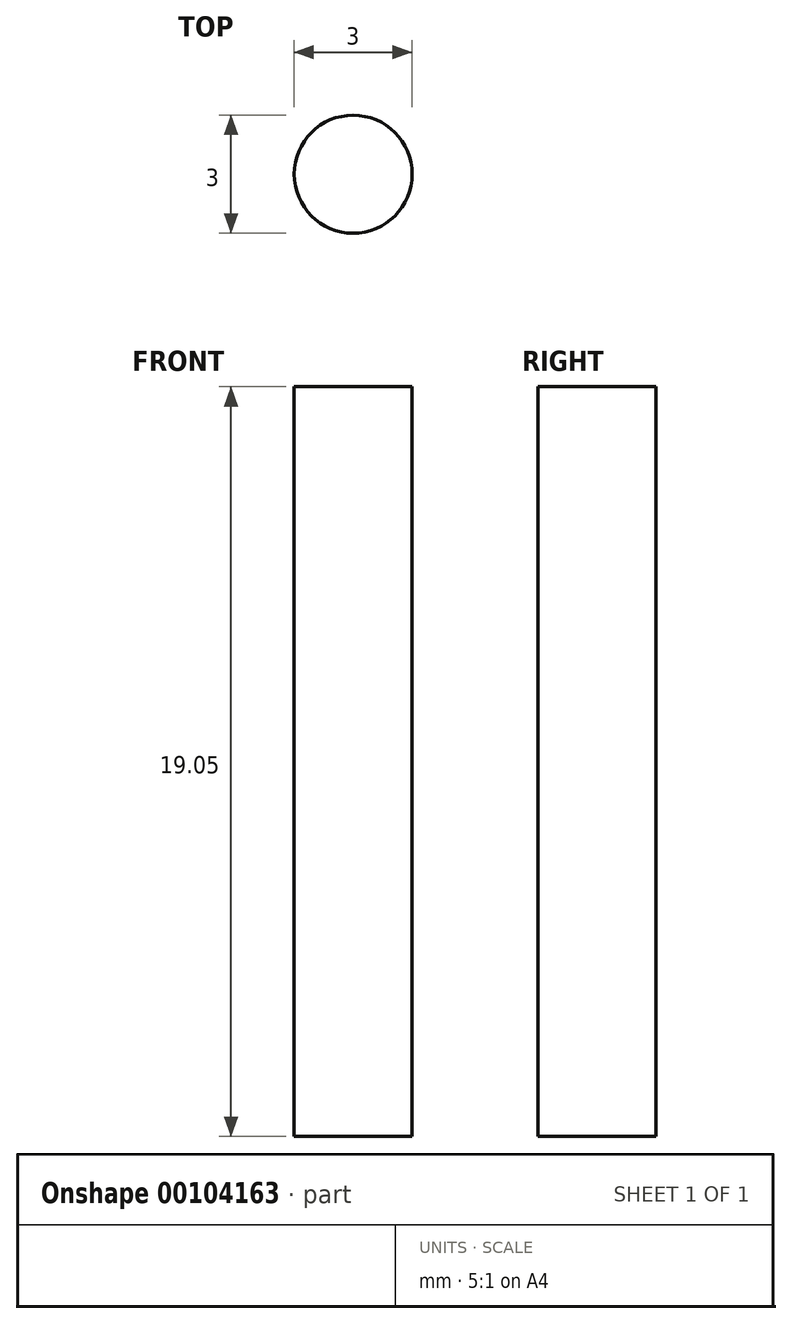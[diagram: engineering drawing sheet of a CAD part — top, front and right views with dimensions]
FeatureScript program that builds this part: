
annotation { "Feature Type Name" : "Feature", "Feature Type Description" : "" }
export const myFeature = defineFeature(function(context is Context, id is Id, definition is map)
    precondition{}
    {
        {
            var Q0;
            Q0=qCreatedBy(makeId("Top.planeOp"),FACE);
            var sketch = newSketch(context, id + "F0", { "sketchPlane" : qUnion([Q0])});
            skCircle(sketch, "E0", {"center": v(-52.28, -17.26) * mm, "radius": 1.5 * mm});
            skSolve(sketch);
        }
        {
            var Q0;
            Q0=makeQuery(id+"F0.imprint","IMPRINT",FACE,{"disambiguationData":[TD([[makeQuery(id+"F0.imprint","IMPRINT",EDGE,{"derivedFrom":sQuery(id+"F0.wireOp",EDGE,"E0")}),1.0]])]});
            extrude(context, id + "F1", {"entities" : qUnion([Q0]), "depth" : 19.05 * mm});
        }
    });
